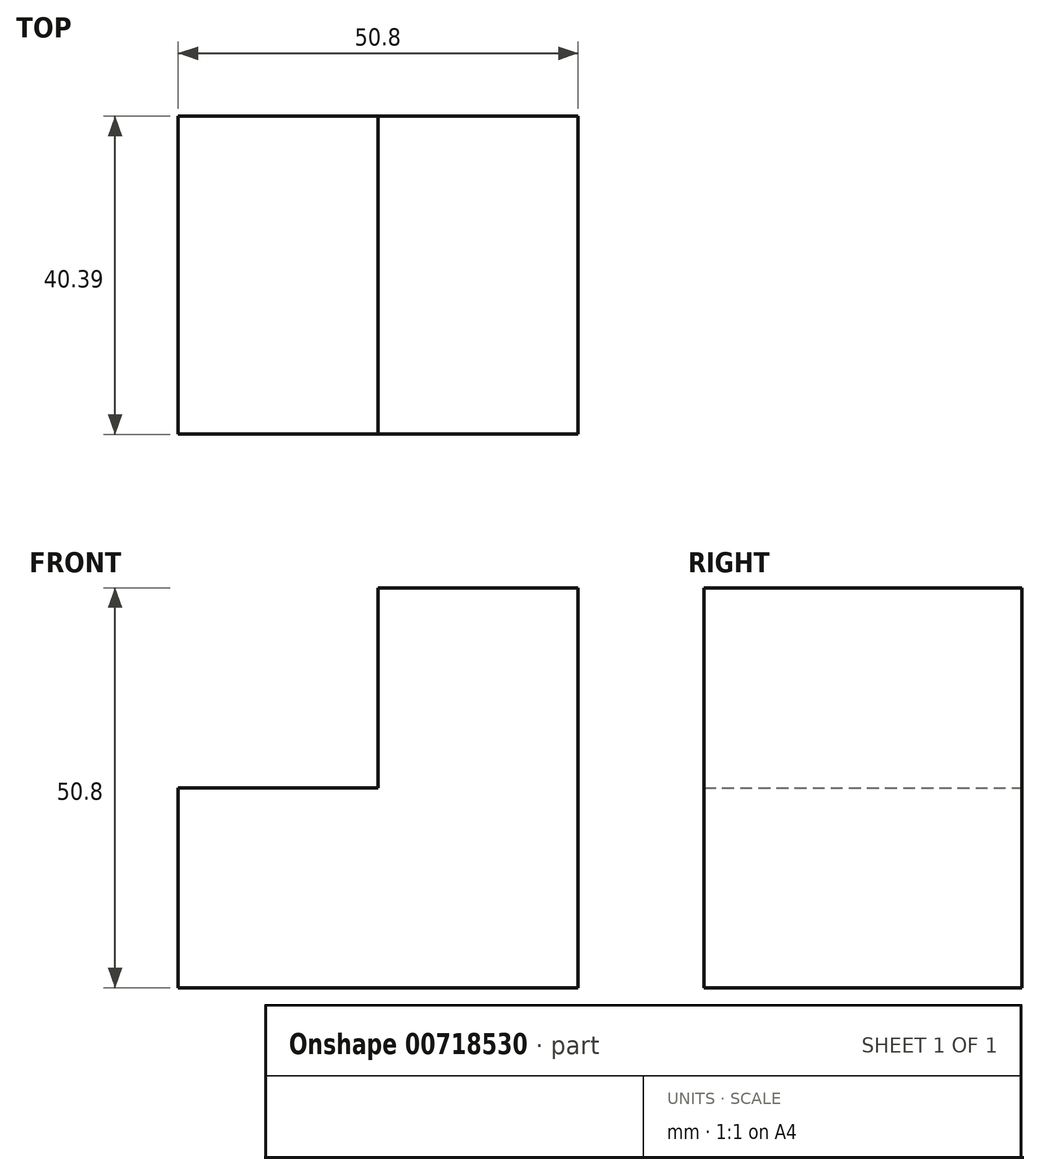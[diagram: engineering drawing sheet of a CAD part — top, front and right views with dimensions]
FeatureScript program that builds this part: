
annotation { "Feature Type Name" : "Feature", "Feature Type Description" : "" }
export const myFeature = defineFeature(function(context is Context, id is Id, definition is map)
    precondition{}
    {
        {
            var Q0;
            Q0=qCreatedBy(makeId("Front.planeOp"),FACE);
            var sketch = newSketch(context, id + "F0", { "sketchPlane" : qUnion([Q0])});
            skLineSegment(sketch, "E0", {"start": v(-25.4, 56.38) * mm, "end": v(0, 56.38) * mm});
            skLineSegment(sketch, "E1", {"start": v(0, 56.38) * mm, "end": v(0, 5.58) * mm});
            skLineSegment(sketch, "E2", {"start": v(0, 5.58) * mm, "end": v(-50.8, 5.58) * mm});
            skLineSegment(sketch, "E3", {"start": v(-50.8, 5.58) * mm, "end": v(-50.8, 30.98) * mm});
            skLineSegment(sketch, "E4", {"start": v(-50.8, 30.98) * mm, "end": v(-25.4, 30.98) * mm});
            skLineSegment(sketch, "E5", {"start": v(-25.4, 30.98) * mm, "end": v(-25.4, 56.38) * mm});
            skSolve(sketch);
        }
        {
            var Q0;
            Q0 = qSketchRegion(id + "F0", true);
            extrude(context, id + "F1", {"entities" : qUnion([Q0]), "depth" : 40.4 * mm, "offsetDistance" : 25.4 * mm});
        }
    });
